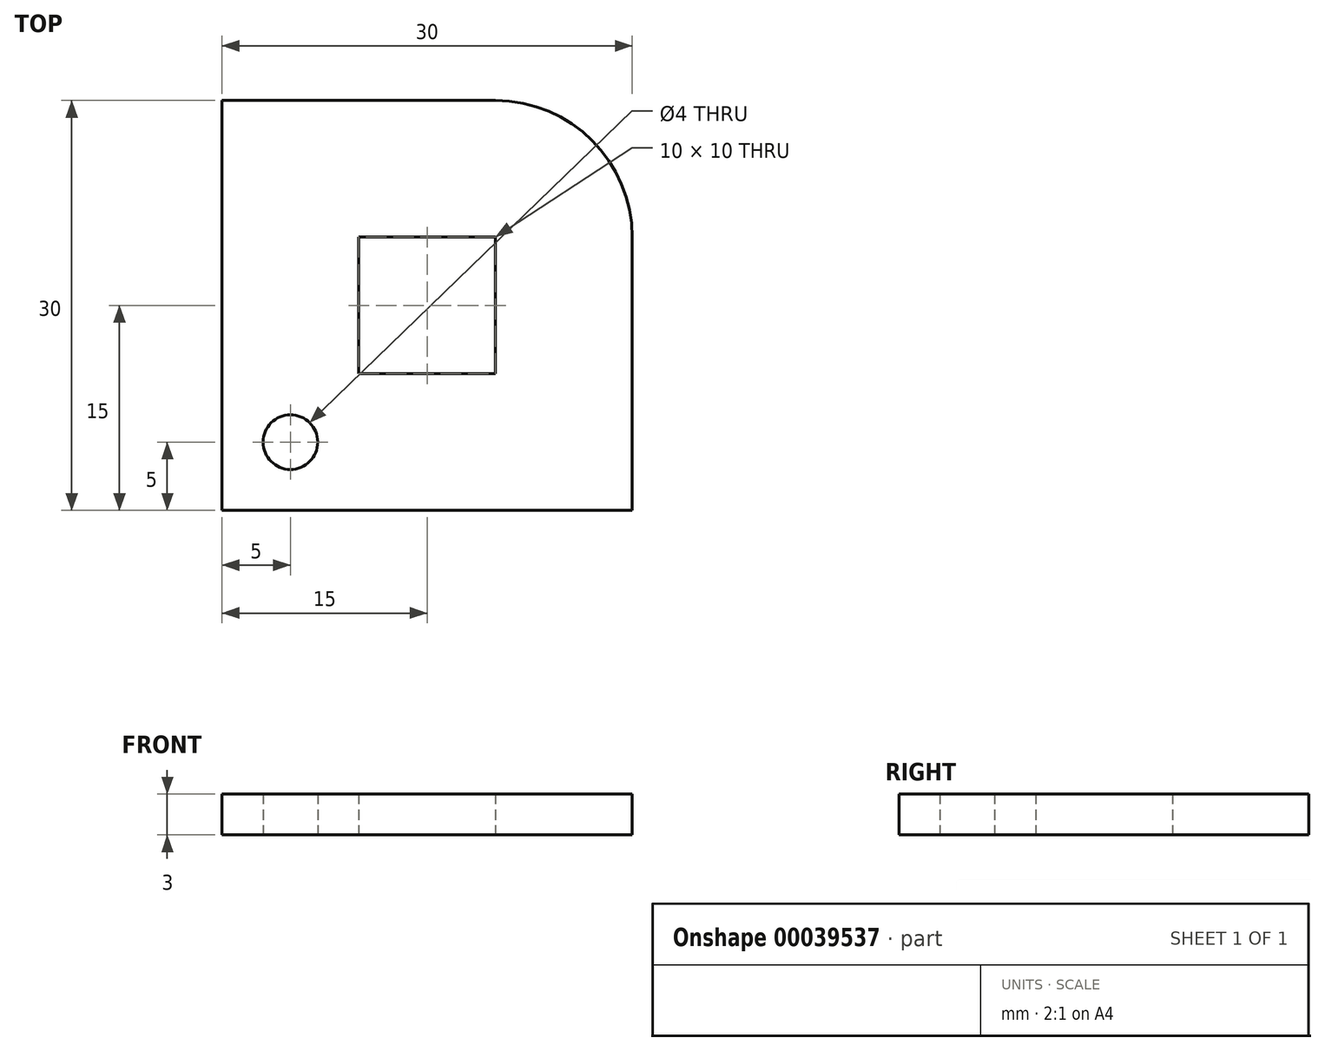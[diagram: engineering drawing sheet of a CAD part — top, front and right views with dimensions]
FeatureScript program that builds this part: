
annotation { "Feature Type Name" : "Feature", "Feature Type Description" : "" }
export const myFeature = defineFeature(function(context is Context, id is Id, definition is map)
    precondition{}
    {
        {
            var Q0;
            Q0=qCreatedBy(makeId("Top.planeOp"),FACE);
            var sketch = newSketch(context, id + "F0", { "sketchPlane" : qUnion([Q0])});
            skLineSegment(sketch, "E0.rect.bottom", {"start": v(15, -15) * mm, "end": v(-15, -15) * mm});
            skLineSegment(sketch, "E0.rect.top", {"start": v(5, 15) * mm, "end": v(-15, 15) * mm});
            skLineSegment(sketch, "E0.rect.left", {"start": v(15, -15) * mm, "end": v(15, 5) * mm});
            skLineSegment(sketch, "E0.rect.right", {"start": v(-15, -15) * mm, "end": v(-15, 15) * mm});
            skPoint(sketch, "E0.rect.middle", {"position": v(0, 0) * mm});
            skLineSegment(sketch, "E1.0", {"start": v(5, 5) * mm, "end": v(-5, 5) * mm});
            skLineSegment(sketch, "E1.1", {"start": v(5, -5) * mm, "end": v(5, 5) * mm});
            skLineSegment(sketch, "E1.2", {"start": v(5, -5) * mm, "end": v(-5, -5) * mm});
            skLineSegment(sketch, "E1.3", {"start": v(-5, -5) * mm, "end": v(-5, 5) * mm});
            skPoint(sketch, "E2.0.visualSharp", {"position": v(15, 15) * mm});
            skArc(sketch, "E2.0.filletArc", {"start": v(15, 5) * mm, "mid": v(12.07, 12.07) * mm, "end": v(5, 15) * mm});
            skLineSegment(sketch, "E3", {"start": v(-15, -15) * mm, "end": v(-5, -5) * mm, "construction": true});
            skCircle(sketch, "E4", {"center": v(-10, -10) * mm, "radius": 2 * mm});
            skSolve(sketch);
        }
        {
            var Q0;
            Q0 = qSketchRegion(id + "F0", true);
            extrude(context, id + "F1", {"entities" : qUnion([Q0]), "depth" : 3 * mm});
        }
    });
